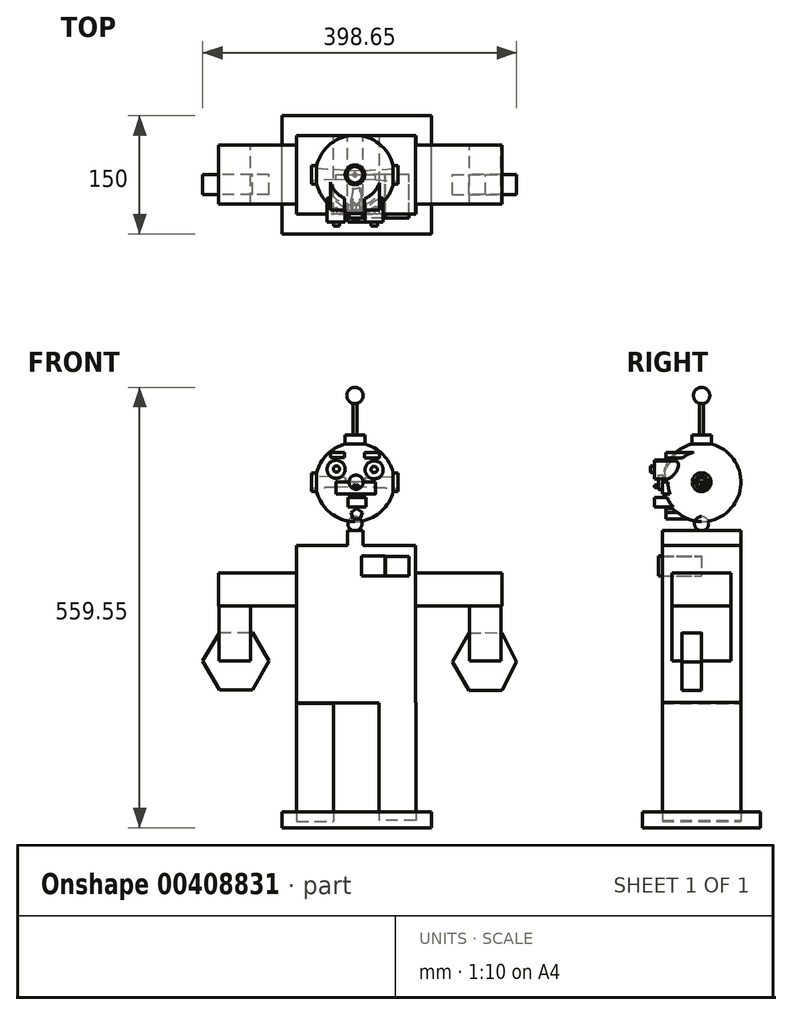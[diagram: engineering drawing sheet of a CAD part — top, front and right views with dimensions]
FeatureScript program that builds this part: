
annotation { "Feature Type Name" : "Feature", "Feature Type Description" : "" }
export const myFeature = defineFeature(function(context is Context, id is Id, definition is map)
    precondition{}
    {
        {
            var Q0;
            Q0=qCreatedBy(makeId("Front.planeOp"),FACE);
            var sketch = newSketch(context, id + "F0", { "sketchPlane" : qUnion([Q0])});
            skArc(sketch, "E0", {"start": v(0, -50) * mm, "mid": v(50, 0) * mm, "end": v(0, 50) * mm});
            skPoint(sketch, "E1", {"position": v(0, 50) * mm});
            skLineSegment(sketch, "E2", {"start": v(0, 50) * mm, "end": v(0, -50) * mm});
            skPoint(sketch, "E3", {"position": v(0, -50) * mm});
            skSolve(sketch);
        }
        {
            var Q0;
            Q0=makeQuery(id+"F0.imprint","IMPRINT",FACE,{"disambiguationData":[TD([[makeQuery(id+"F0.imprint","IMPRINT",EDGE,{"derivedFrom":sQuery(id+"F0.wireOp",EDGE,"E0")}),1.0]])]});
            var Q1;
            Q1=sQuery(id+"F0.wireOp",EDGE,"E2");
            revolve(context, id + "F1", {"entities" : qUnion([Q0]), "axis" : qUnion([Q1]), "revolveType" : RevolveType.FULL});
        }
        {
            var Q0;
            Q0=qCreatedBy(makeId("Front.planeOp"),FACE);
            var sketch = newSketch(context, id + "F2", { "sketchPlane" : qUnion([Q0])});
            skCircle(sketch, "E4", {"center": v(-23.9, 16.41) * mm, "radius": 11.5 * mm});
            skCircle(sketch, "E5", {"center": v(24.4, 15.66) * mm, "radius": 11.5 * mm});
            skSolve(sketch);
        }
        {
            var Q0;
            Q0 = qSketchRegion(id + "F2", true);
            extrude(context, id + "F3", {"entities" : qUnion([Q0]), "operationType" : NewBodyOperationType.ADD, "depth" : 60 * mm});
        }
        {
            var Q0;
            Q0=qCreatedBy(makeId("Front.planeOp"),FACE);
            var sketch = newSketch(context, id + "F4", { "sketchPlane" : qUnion([Q0])});
            skPoint(sketch, "E6", {"position": v(-23.46, 16.75) * mm});
            skPoint(sketch, "E7", {"position": v(24.45, 16.15) * mm});
            skCircle(sketch, "E8", {"center": v(-23.46, 16.75) * mm, "radius": 4 * mm});
            skCircle(sketch, "E9", {"center": v(24.45, 16.15) * mm, "radius": 4 * mm});
            skSolve(sketch);
        }
        {
            var Q0;
            Q0 = qSketchRegion(id + "F4", true);
            extrude(context, id + "F5", {"entities" : qUnion([Q0]), "operationType" : NewBodyOperationType.ADD, "depth" : 65 * mm, "offsetDistance" : 25 * mm});
        }
        {
            var Q0;
            Q0=qCreatedBy(makeId("Front.planeOp"),FACE);
            var sketch = newSketch(context, id + "F6", { "sketchPlane" : qUnion([Q0])});
            skCircle(sketch, "E10", {"center": v(1.45, 0) * mm, "radius": 9 * mm});
            skSolve(sketch);
        }
        {
            var Q0;
            Q0 = qSketchRegion(id + "F6", true);
            extrude(context, id + "F7", {"entities" : qUnion([Q0]), "operationType" : NewBodyOperationType.ADD, "depth" : 55 * mm, "offsetDistance" : 25 * mm});
        }
        {
            var Q0;
            Q0=qCreatedBy(makeId("Front.planeOp"),FACE);
            var sketch = newSketch(context, id + "F8", { "sketchPlane" : qUnion([Q0])});
            skLineSegment(sketch, "E11.bottom", {"start": v(14.25, -31.74) * mm, "end": v(-8.75, -31.74) * mm});
            skLineSegment(sketch, "E11.top", {"start": v(14.25, -19.37) * mm, "end": v(-8.75, -19.37) * mm});
            skLineSegment(sketch, "E11.left", {"start": v(14.25, -31.74) * mm, "end": v(14.25, -19.37) * mm});
            skLineSegment(sketch, "E11.right", {"start": v(-8.75, -31.74) * mm, "end": v(-8.75, -19.37) * mm});
            skSolve(sketch);
        }
        {
            var Q0;
            Q0 = qSketchRegion(id + "F8", true);
            extrude(context, id + "F9", {"entities" : qUnion([Q0]), "operationType" : NewBodyOperationType.ADD, "depth" : 60 * mm});
        }
        {
            var Q0;
            Q0=qCreatedBy(makeId("Front.planeOp"),FACE);
            var sketch = newSketch(context, id + "F10", { "sketchPlane" : qUnion([Q0])});
            skLineSegment(sketch, "E12.bottom", {"start": v(-31.3, 31.3) * mm, "end": v(-13.27, 31.3) * mm});
            skLineSegment(sketch, "E12.top", {"start": v(-31.3, 37.84) * mm, "end": v(-13.27, 37.84) * mm});
            skLineSegment(sketch, "E12.left", {"start": v(-31.3, 31.3) * mm, "end": v(-31.3, 37.84) * mm});
            skLineSegment(sketch, "E12.right", {"start": v(-13.27, 31.3) * mm, "end": v(-13.27, 37.84) * mm});
            skLineSegment(sketch, "E13.bottom", {"start": v(12.3, 37.84) * mm, "end": v(30.91, 37.84) * mm});
            skLineSegment(sketch, "E13.top", {"start": v(12.3, 30.9) * mm, "end": v(30.91, 30.9) * mm});
            skLineSegment(sketch, "E13.left", {"start": v(12.3, 37.84) * mm, "end": v(12.3, 30.9) * mm});
            skLineSegment(sketch, "E13.right", {"start": v(30.91, 37.84) * mm, "end": v(30.91, 30.9) * mm});
            skSolve(sketch);
        }
        {
            var Q0;
            Q0 = qSketchRegion(id + "F10", true);
            extrude(context, id + "F11", {"entities" : qUnion([Q0]), "operationType" : NewBodyOperationType.ADD, "depth" : 45 * mm});
        }
        {
            var Q0;
            Q0=qCreatedBy(makeId("Right.planeOp"),FACE);
            var sketch = newSketch(context, id + "F12", { "sketchPlane" : qUnion([Q0])});
            skCircle(sketch, "E14", {"center": v(0, 0) * mm, "radius": 12 * mm});
            skSolve(sketch);
        }
        {
            var Q0;
            Q0 = qSketchRegion(id + "F12", true);
            extrude(context, id + "F13", {"entities" : qUnion([Q0]), "operationType" : NewBodyOperationType.ADD, "oppositeDirection" : true, "depth" : 55 * mm});
        }
        {
            var Q0;
            Q0=qCreatedBy(makeId("Right.planeOp"),FACE);
            var sketch = newSketch(context, id + "F14", { "sketchPlane" : qUnion([Q0])});
            skCircle(sketch, "E15", {"center": v(0, 0) * mm, "radius": 12 * mm});
            skSolve(sketch);
        }
        {
            var Q0;
            Q0 = qSketchRegion(id + "F14", true);
            extrude(context, id + "F15", {"entities" : qUnion([Q0]), "operationType" : NewBodyOperationType.ADD, "depth" : 55 * mm});
        }
        {
            var Q0;
            Q0=qCreatedBy(makeId("Right.planeOp"),FACE);
            var sketch = newSketch(context, id + "F16", { "sketchPlane" : qUnion([Q0])});
            skCircle(sketch, "E16", {"center": v(0, 0) * mm, "radius": 5 * mm});
            skSolve(sketch);
        }
        {
            var Q0;
            Q0 = qSketchRegion(id + "F16", true);
            extrude(context, id + "F17", {"entities" : qUnion([Q0]), "operationType" : NewBodyOperationType.REMOVE, "depth" : 55 * mm, "hasDraft" : true, "draftAngle" : 3 * degree});
        }
        {
            var Q0;
            Q0=qCreatedBy(makeId("Right.planeOp"),FACE);
            var sketch = newSketch(context, id + "F18", { "sketchPlane" : qUnion([Q0])});
            skCircle(sketch, "E17", {"center": v(0, 0) * mm, "radius": 5 * mm});
            skSolve(sketch);
        }
        {
            var Q0;
            Q0 = qSketchRegion(id + "F18", true);
            extrude(context, id + "F19", {"entities" : qUnion([Q0]), "operationType" : NewBodyOperationType.REMOVE, "oppositeDirection" : true, "depth" : 55 * mm, "hasDraft" : true, "draftAngle" : 3 * degree});
        }
        {
            var Q0;
            Q0=qCreatedBy(makeId("Front.planeOp"),FACE);
            var sketch = newSketch(context, id + "F20", { "sketchPlane" : qUnion([Q0])});
            skLineSegment(sketch, "E18.bottom", {"start": v(-24.07, 0) * mm, "end": v(25.93, 0) * mm});
            skLineSegment(sketch, "E18.top", {"start": v(-24.07, -15) * mm, "end": v(25.93, -15) * mm});
            skLineSegment(sketch, "E18.left", {"start": v(-24.07, 0) * mm, "end": v(-24.07, -15) * mm});
            skLineSegment(sketch, "E18.right", {"start": v(25.93, 0) * mm, "end": v(25.93, -15) * mm});
            skSolve(sketch);
        }
        {
            var Q0;
            Q0 = qSketchRegion(id + "F20", true);
            extrude(context, id + "F21", {"entities" : qUnion([Q0]), "operationType" : NewBodyOperationType.ADD, "depth" : 50 * mm});
        }
        {
            var Q0;
            Q0=qCreatedBy(makeId("Front.planeOp"),FACE);
            var sketch = newSketch(context, id + "F22", { "sketchPlane" : qUnion([Q0])});
            skCircle(sketch, "E19", {"center": v(-0.73, -5.15) * mm, "radius": 1.5 * mm});
            skCircle(sketch, "E20", {"center": v(3.27, -5.15) * mm, "radius": 1.5 * mm});
            skSolve(sketch);
        }
        {
            var Q0;
            Q0 = qSketchRegion(id + "F22", true);
            extrude(context, id + "F23", {"entities" : qUnion([Q0]), "operationType" : NewBodyOperationType.ADD, "depth" : 60 * mm});
        }
        {
            var Q0;
            Q0=qCreatedBy(makeId("Top.planeOp"),FACE);
            var sketch = newSketch(context, id + "F24", { "sketchPlane" : qUnion([Q0])});
            skCircle(sketch, "E21", {"center": v(0, 0) * mm, "radius": 12.5 * mm});
            skSolve(sketch);
        }
        {
            var Q0;
            Q0 = qSketchRegion(id + "F24", true);
            extrude(context, id + "F25", {"entities" : qUnion([Q0]), "operationType" : NewBodyOperationType.ADD, "depth" : 60 * mm});
        }
        {
            var Q0;
            Q0=qCreatedBy(makeId("Top.planeOp"),FACE);
            var sketch = newSketch(context, id + "F26", { "sketchPlane" : qUnion([Q0])});
            skCircle(sketch, "E22", {"center": v(0, 0) * mm, "radius": 2.5 * mm});
            skSolve(sketch);
        }
        {
            var Q0;
            Q0 = qSketchRegion(id + "F26", true);
            extrude(context, id + "F27", {"entities" : qUnion([Q0]), "operationType" : NewBodyOperationType.ADD, "depth" : 100 * mm});
        }
        {
            var Q0;
            Q0=qCreatedBy(makeId("Front.planeOp"),FACE);
            var sketch = newSketch(context, id + "F28", { "sketchPlane" : qUnion([Q0])});
            skPoint(sketch, "E23", {"position": v(0, 110.17) * mm});
            skArc(sketch, "E24", {"start": v(0, 99.77) * mm, "mid": v(10.4, 110.17) * mm, "end": v(0, 120.56) * mm});
            skLineSegment(sketch, "E25", {"start": v(0, 120.56) * mm, "end": v(0, 99.77) * mm});
            skSolve(sketch);
        }
        {
            var Q0;
            Q0 = qSketchRegion(id + "F28", true);
            var Q1;
            Q1=sQuery(id+"F28.wireOp",EDGE,"E25");
            revolve(context, id + "F29", {"entities" : qUnion([Q0]), "axis" : qUnion([Q1]), "revolveType" : RevolveType.FULL});
        }
        {
            var Q0;
            Q0=qCreatedBy(makeId("Front.planeOp"),FACE);
            var sketch = newSketch(context, id + "F30", { "sketchPlane" : qUnion([Q0])});
            skCircle(sketch, "E26.cCircle", {"center": v(2.13, -40.72) * mm, "radius": 6.2 * mm, "construction": true});
            skLineSegment(sketch, "E26.0", {"start": v(6.63, -46.92) * mm, "end": v(-2.37, -46.92) * mm});
            skLineSegment(sketch, "E26.1", {"start": v(-2.37, -46.92) * mm, "end": v(-5.15, -38.36) * mm});
            skLineSegment(sketch, "E26.2", {"start": v(-5.15, -38.36) * mm, "end": v(2.13, -33.07) * mm});
            skLineSegment(sketch, "E26.3", {"start": v(2.13, -33.07) * mm, "end": v(9.41, -38.36) * mm});
            skLineSegment(sketch, "E26.4", {"start": v(9.41, -38.36) * mm, "end": v(6.63, -46.92) * mm});
            skPoint(sketch, "E26.0.midPoint", {"position": v(2.13, -46.92) * mm});
            skSolve(sketch);
        }
        {
            var Q0;
            Q0 = qSketchRegion(id + "F30", true);
            extrude(context, id + "F31", {"entities" : qUnion([Q0]), "operationType" : NewBodyOperationType.ADD, "depth" : 45 * mm});
        }
        {
            var Q0;
            Q0=qCreatedBy(makeId("Front.planeOp"),FACE);
            var sketch = newSketch(context, id + "F32", { "sketchPlane" : qUnion([Q0])});
            skArc(sketch, "E27", {"start": v(0, -61.65) * mm, "mid": v(9, -52.65) * mm, "end": v(0, -43.65) * mm});
            skLineSegment(sketch, "E28", {"start": v(0, -43.65) * mm, "end": v(0, -61.65) * mm});
            skSolve(sketch);
        }
        {
            var Q0;
            Q0 = qSketchRegion(id + "F32", true);
            var Q1;
            Q1=sQuery(id+"F32.wireOp",EDGE,"E28");
            revolve(context, id + "F33", {"entities" : qUnion([Q0]), "axis" : qUnion([Q1]), "revolveType" : RevolveType.FULL});
        }
        {
            var Q0;
            Q0=qCreatedBy(makeId("Front.planeOp"),FACE);
            var sketch = newSketch(context, id + "F34", { "sketchPlane" : qUnion([Q0])});
            skLineSegment(sketch, "E29.bottom", {"start": v(76.76, -80.52) * mm, "end": v(-74.24, -80.52) * mm});
            skLineSegment(sketch, "E29.top", {"start": v(76.76, -280.52) * mm, "end": v(-74.24, -280.52) * mm});
            skLineSegment(sketch, "E29.left", {"start": v(76.76, -80.52) * mm, "end": v(76.76, -280.52) * mm});
            skLineSegment(sketch, "E29.right", {"start": v(-74.24, -80.52) * mm, "end": v(-74.24, -280.52) * mm});
            skLineSegment(sketch, "E30.bottom", {"start": v(-9.6, -61.52) * mm, "end": v(10.4, -61.52) * mm});
            skLineSegment(sketch, "E30.top", {"start": v(-9.6, -80.52) * mm, "end": v(10.4, -80.52) * mm});
            skLineSegment(sketch, "E30.left", {"start": v(-9.6, -61.52) * mm, "end": v(-9.6, -80.52) * mm});
            skLineSegment(sketch, "E30.right", {"start": v(10.4, -61.52) * mm, "end": v(10.4, -80.52) * mm});
            skSolve(sketch);
        }
        {
            var Q0;
            Q0 = qSketchRegion(id + "F34", true);
            extrude(context, id + "F35", {"entities" : qUnion([Q0]), "operationType" : NewBodyOperationType.ADD, "endBound" : BoundingType.SYMMETRIC, "depth" : 100 * mm});
        }
        {
            var Q0;
            Q0=qCreatedBy(makeId("Front.planeOp"),FACE);
            var sketch = newSketch(context, id + "F36", { "sketchPlane" : qUnion([Q0])});
            skLineSegment(sketch, "E31.bottom", {"start": v(76.84, -115.23) * mm, "end": v(186.84, -115.23) * mm});
            skLineSegment(sketch, "E31.top", {"start": v(76.84, -157.23) * mm, "end": v(186.84, -157.23) * mm});
            skLineSegment(sketch, "E31.left", {"start": v(76.84, -115.23) * mm, "end": v(76.84, -157.23) * mm});
            skLineSegment(sketch, "E31.right", {"start": v(186.84, -115.23) * mm, "end": v(186.84, -157.23) * mm});
            skLineSegment(sketch, "E32.bottom", {"start": v(-73.5, -115.23) * mm, "end": v(-173.5, -115.23) * mm});
            skLineSegment(sketch, "E32.top", {"start": v(-73.5, -157.23) * mm, "end": v(-173.5, -157.23) * mm});
            skLineSegment(sketch, "E32.left", {"start": v(-73.5, -115.23) * mm, "end": v(-73.5, -157.23) * mm});
            skLineSegment(sketch, "E32.right", {"start": v(-173.5, -115.23) * mm, "end": v(-173.5, -157.23) * mm});
            skSolve(sketch);
        }
        {
            var Q0;
            Q0 = qSketchRegion(id + "F36", true);
            extrude(context, id + "F37", {"entities" : qUnion([Q0]), "endBound" : BoundingType.SYMMETRIC, "depth" : 75 * mm});
        }
        {
            var Q0;
            Q0=qCreatedBy(makeId("Front.planeOp"),FACE);
            var sketch = newSketch(context, id + "F38", { "sketchPlane" : qUnion([Q0])});
            skLineSegment(sketch, "E33.bottom", {"start": v(-172.8, -156.98) * mm, "end": v(-132.8, -156.98) * mm});
            skLineSegment(sketch, "E33.top", {"start": v(-172.8, -226.98) * mm, "end": v(-132.8, -226.98) * mm});
            skLineSegment(sketch, "E33.left", {"start": v(-172.8, -156.98) * mm, "end": v(-172.8, -226.98) * mm});
            skLineSegment(sketch, "E33.right", {"start": v(-132.8, -156.98) * mm, "end": v(-132.8, -226.98) * mm});
            skLineSegment(sketch, "E34.bottom", {"start": v(185.35, -156.98) * mm, "end": v(145.35, -156.98) * mm});
            skLineSegment(sketch, "E34.top", {"start": v(185.35, -226.98) * mm, "end": v(145.35, -226.98) * mm});
            skLineSegment(sketch, "E34.left", {"start": v(185.35, -156.98) * mm, "end": v(185.35, -226.98) * mm});
            skLineSegment(sketch, "E34.right", {"start": v(145.35, -156.98) * mm, "end": v(145.35, -226.98) * mm});
            skSolve(sketch);
        }
        {
            var Q0;
            Q0 = qSketchRegion(id + "F38", true);
            extrude(context, id + "F39", {"entities" : qUnion([Q0]), "endBound" : BoundingType.SYMMETRIC, "depth" : 75 * mm});
        }
        {
            var Q0;
            Q0=qCreatedBy(makeId("Front.planeOp"),FACE);
            var sketch = newSketch(context, id + "F40", { "sketchPlane" : qUnion([Q0])});
            skLineSegment(sketch, "E35.bottom", {"start": v(68.77, -94.05) * mm, "end": v(53.77, -94.05) * mm});
            skLineSegment(sketch, "E35.top", {"start": v(68.77, -119.05) * mm, "end": v(53.77, -119.05) * mm});
            skLineSegment(sketch, "E35.left", {"start": v(68.77, -94.05) * mm, "end": v(68.77, -119.05) * mm});
            skLineSegment(sketch, "E35.right", {"start": v(53.77, -94.05) * mm, "end": v(53.77, -119.05) * mm});
            skLineSegment(sketch, "E36.bottom", {"start": v(53.77, -94.05) * mm, "end": v(38.77, -94.05) * mm});
            skLineSegment(sketch, "E36.top", {"start": v(53.77, -119.05) * mm, "end": v(38.77, -119.05) * mm});
            skLineSegment(sketch, "E36.right", {"start": v(38.77, -94.05) * mm, "end": v(38.77, -119.05) * mm});
            skSolve(sketch);
        }
        {
            var Q0;
            Q0 = qSketchRegion(id + "F40", true);
            extrude(context, id + "F41", {"entities" : qUnion([Q0]), "depth" : 55 * mm});
        }
        {
            var Q0;
            Q0=qCreatedBy(makeId("Front.planeOp"),FACE);
            var sketch = newSketch(context, id + "F42", { "sketchPlane" : qUnion([Q0])});
            skLineSegment(sketch, "E37.bottom", {"start": v(38.13, -94) * mm, "end": v(8.13, -94) * mm});
            skLineSegment(sketch, "E37.top", {"start": v(38.13, -119) * mm, "end": v(8.13, -119) * mm});
            skLineSegment(sketch, "E37.left", {"start": v(38.13, -94) * mm, "end": v(38.13, -119) * mm});
            skLineSegment(sketch, "E37.right", {"start": v(8.13, -94) * mm, "end": v(8.13, -119) * mm});
            skSolve(sketch);
        }
        {
            var Q0;
            Q0 = qSketchRegion(id + "F42", true);
            extrude(context, id + "F43", {"entities" : qUnion([Q0]), "depth" : 55 * mm});
        }
        {
            var Q0;
            Q0=makeQuery(id+"F21.opExtrude","CAP_EDGE",EDGE,{"disambiguationData":[OSD([sQuery(id+"F20.wireOp",EDGE,"E18.left")])],"isStart":false});
            var Q1;
            Q1=makeQuery(id+"F21.opExtrude","CAP_EDGE",EDGE,{"disambiguationData":[OSD([sQuery(id+"F20.wireOp",EDGE,"E18.right")])],"isStart":false});
            fillet(context, id + "F44", {"entities" : qUnion([Q0, Q1]), "radius" : 5 * mm, "tangentPropagation" : true, "allowEdgeOverflow" : false});
        }
        {
            var Q0;
            Q0=qCreatedBy(makeId("Front.planeOp"),FACE);
            var sketch = newSketch(context, id + "F45", { "sketchPlane" : qUnion([Q0])});
            skArc(sketch, "E38.cCircle", {"start": v(-151.28, -190.95) * mm, "mid": v(-187.65, -227.32) * mm, "end": v(-151.28, -263.7) * mm, "construction": true});
            skLineSegment(sketch, "E38.0", {"start": v(-151.28, -263.7) * mm, "end": v(-172.28, -263.7) * mm});
            skLineSegment(sketch, "E38.1", {"start": v(-172.28, -263.7) * mm, "end": v(-193.28, -227.32) * mm});
            skLineSegment(sketch, "E38.2", {"start": v(-193.28, -227.32) * mm, "end": v(-172.28, -190.95) * mm});
            skLineSegment(sketch, "E38.3", {"start": v(-172.28, -190.95) * mm, "end": v(-151.28, -190.95) * mm});
            skPoint(sketch, "E38.0.midPoint", {"position": v(-151.28, -263.7) * mm});
            skArc(sketch, "E39.cCircle", {"start": v(165.6, -191.74) * mm, "mid": v(129.22, -228.1) * mm, "end": v(165.6, -264.48) * mm, "construction": true});
            skLineSegment(sketch, "E39.0", {"start": v(165.6, -264.48) * mm, "end": v(144.6, -264.48) * mm});
            skLineSegment(sketch, "E39.1", {"start": v(144.6, -264.48) * mm, "end": v(123.6, -228.1) * mm});
            skLineSegment(sketch, "E39.2", {"start": v(123.6, -228.1) * mm, "end": v(144.6, -191.74) * mm});
            skLineSegment(sketch, "E39.3", {"start": v(144.6, -191.74) * mm, "end": v(165.6, -191.74) * mm});
            skPoint(sketch, "E39.0.midPoint", {"position": v(165.6, -264.48) * mm});
            skLineSegment(sketch, "E40", {"start": v(-151.28, -190.95) * mm, "end": v(-151.28, -263.7) * mm});
            skLineSegment(sketch, "E41", {"start": v(165.6, -190.95) * mm, "end": v(165.6, -264.48) * mm});
            skPoint(sketch, "E41.startSnap0", {"position": v(165.6, -191.74) * mm});
            skPoint(sketch, "E42.orphan", {"position": v(-109.28, -227.32) * mm});
            skPoint(sketch, "E43.orphan", {"position": v(-130.28, -263.7) * mm});
            skPoint(sketch, "E44.orphan", {"position": v(-130.28, -190.95) * mm});
            skPoint(sketch, "E39.5.end.orphan", {"position": v(186.6, -264.48) * mm});
            skPoint(sketch, "E45.orphan", {"position": v(186.6, -191.74) * mm});
            skLineSegment(sketch, "E46", {"start": v(-151.28, -190.95) * mm, "end": v(-130.28, -190.95) * mm});
            skLineSegment(sketch, "E47", {"start": v(-130.28, -190.95) * mm, "end": v(-109.28, -227.32) * mm});
            skLineSegment(sketch, "E48", {"start": v(-109.28, -227.32) * mm, "end": v(-130.28, -263.7) * mm});
            skLineSegment(sketch, "E49", {"start": v(-130.28, -263.7) * mm, "end": v(-151.28, -263.7) * mm});
            skLineSegment(sketch, "E50", {"start": v(165.6, -190.95) * mm, "end": v(186.6, -191.74) * mm});
            skLineSegment(sketch, "E51", {"start": v(165.6, -264.48) * mm, "end": v(186.6, -264.48) * mm});
            skPoint(sketch, "E52", {"position": v(205.37, -228.1) * mm});
            skPoint(sketch, "E52.positionSnap0", {"position": v(129.22, -228.1) * mm});
            skLineSegment(sketch, "E53", {"start": v(186.6, -191.74) * mm, "end": v(205.37, -228.1) * mm});
            skLineSegment(sketch, "E54", {"start": v(186.6, -264.48) * mm, "end": v(205.37, -228.1) * mm});
            skSolve(sketch);
        }
        {
            var Q0;
            Q0 = qSketchRegion(id + "F45", true);
            extrude(context, id + "F46", {"entities" : qUnion([Q0]), "depth" : 25 * mm, "offsetDistance" : 25 * mm});
        }
        {
            var Q0;
            Q0=qCreatedBy(makeId("Front.planeOp"),FACE);
            var sketch = newSketch(context, id + "F47", { "sketchPlane" : qUnion([Q0])});
            skLineSegment(sketch, "E55.bottom", {"start": v(-74.21, -280.93) * mm, "end": v(-27.21, -280.93) * mm});
            skLineSegment(sketch, "E55.top", {"start": v(-74.21, -430.93) * mm, "end": v(-27.21, -430.93) * mm});
            skLineSegment(sketch, "E55.left", {"start": v(-74.21, -280.93) * mm, "end": v(-74.21, -430.93) * mm});
            skLineSegment(sketch, "E55.right", {"start": v(-27.21, -280.93) * mm, "end": v(-27.21, -430.93) * mm});
            skLineSegment(sketch, "E56.bottom", {"start": v(77.32, -279.54) * mm, "end": v(30.32, -279.54) * mm});
            skLineSegment(sketch, "E56.top", {"start": v(77.32, -429.54) * mm, "end": v(30.32, -429.54) * mm});
            skLineSegment(sketch, "E56.left", {"start": v(77.32, -279.54) * mm, "end": v(77.32, -429.54) * mm});
            skLineSegment(sketch, "E56.right", {"start": v(30.32, -279.54) * mm, "end": v(30.32, -429.54) * mm});
            skSolve(sketch);
        }
        {
            var Q0;
            Q0 = qSketchRegion(id + "F47", true);
            extrude(context, id + "F48", {"entities" : qUnion([Q0]), "operationType" : NewBodyOperationType.ADD, "endBound" : BoundingType.SYMMETRIC, "depth" : 100 * mm, "offsetDistance" : 25 * mm});
        }
        {
            var Q0;
            Q0=qCreatedBy(makeId("Front.planeOp"),FACE);
            var sketch = newSketch(context, id + "F49", { "sketchPlane" : qUnion([Q0])});
            skLineSegment(sketch, "E57.bottom", {"start": v(-92.85, -419) * mm, "end": v(97.15, -419) * mm});
            skLineSegment(sketch, "E57.top", {"start": v(-92.85, -439) * mm, "end": v(97.15, -439) * mm});
            skLineSegment(sketch, "E57.left", {"start": v(-92.85, -419) * mm, "end": v(-92.85, -439) * mm});
            skLineSegment(sketch, "E57.right", {"start": v(97.15, -419) * mm, "end": v(97.15, -439) * mm});
            skSolve(sketch);
        }
        {
            var Q0;
            Q0 = qSketchRegion(id + "F49", true);
            extrude(context, id + "F50", {"entities" : qUnion([Q0]), "endBound" : BoundingType.SYMMETRIC, "depth" : 150 * mm, "offsetDistance" : 25 * mm});
        }
    });
